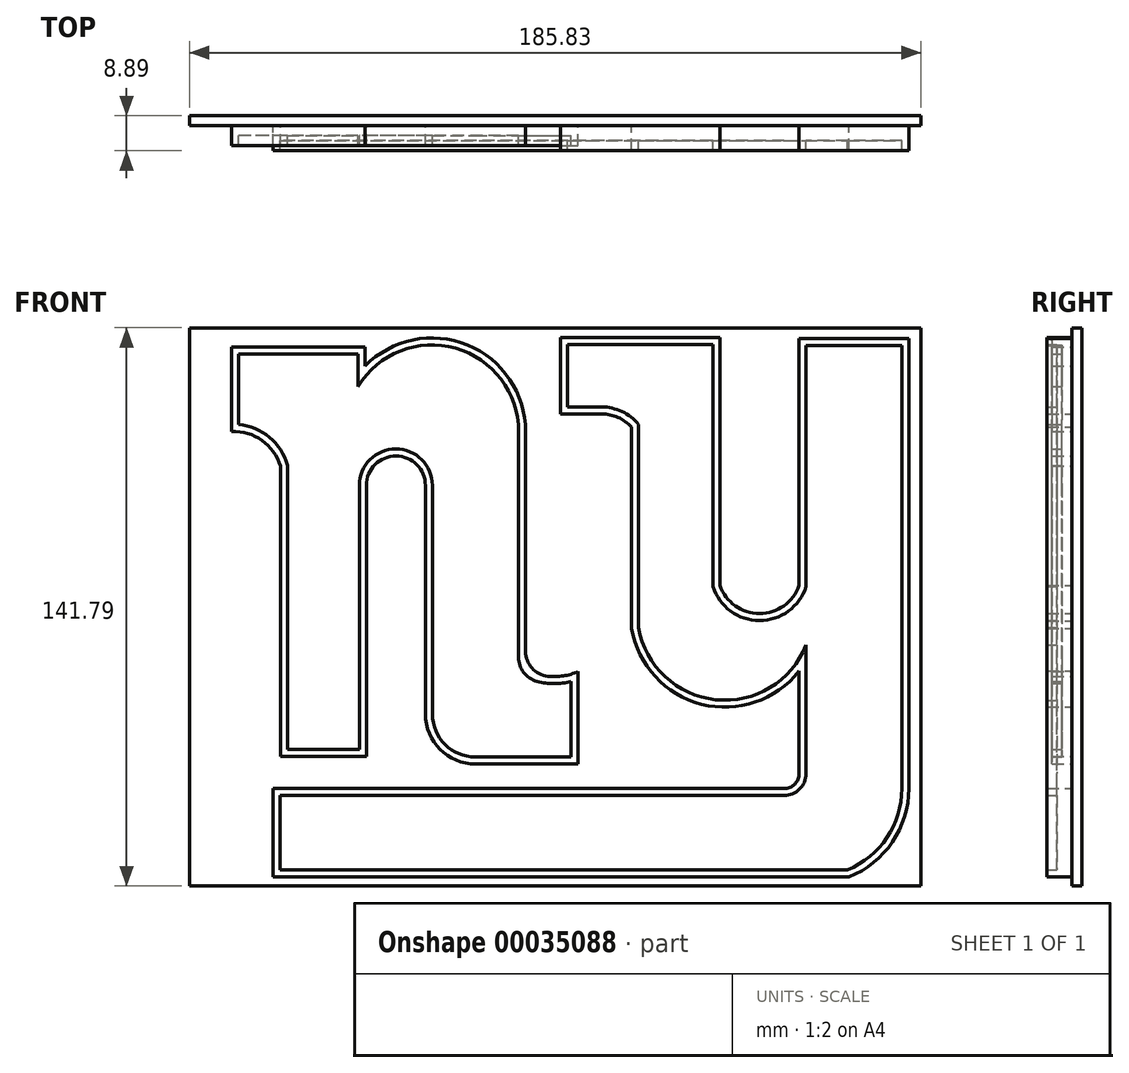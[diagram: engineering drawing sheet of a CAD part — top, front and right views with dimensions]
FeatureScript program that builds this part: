
annotation { "Feature Type Name" : "Feature", "Feature Type Description" : "" }
export const myFeature = defineFeature(function(context is Context, id is Id, definition is map)
    precondition{}
    {
        {
            var Q0;
            Q0=qCreatedBy(makeId("Front.planeOp"),FACE);
            var sketch = newSketch(context, id + "F0", { "sketchPlane" : qUnion([Q0])});
            skLineSegment(sketch, "E0", {"start": v(-67.96, -59.93) * mm, "end": v(61.89, -59.93) * mm});
            skLineSegment(sketch, "E1", {"start": v(-67.96, -59.93) * mm, "end": v(-67.96, -82.39) * mm});
            skLineSegment(sketch, "E2", {"start": v(-67.96, -82.39) * mm, "end": v(78.3, -82.39) * mm});
            skLineSegment(sketch, "E3", {"start": v(65.7, -56.12) * mm, "end": v(65.7, -30.07) * mm});
            skPoint(sketch, "E4.visualSharp", {"position": v(65.7, -59.93) * mm});
            skArc(sketch, "E4.filletArc", {"start": v(61.89, -59.93) * mm, "mid": v(64.58, -58.81) * mm, "end": v(65.7, -56.12) * mm});
            skLineSegment(sketch, "E5", {"start": v(23.13, -19.2) * mm, "end": v(23.13, 31.92) * mm});
            skLineSegment(sketch, "E6", {"start": v(93.56, -59.93) * mm, "end": v(93.56, 54.43) * mm});
            skLineSegment(sketch, "E7", {"start": v(65.7, 54.43) * mm, "end": v(65.7, -8.29) * mm});
            skPoint(sketch, "E7.startSnap0", {"position": v(58.35, 54.43) * mm});
            skLineSegment(sketch, "E8", {"start": v(45.58, 54.7) * mm, "end": v(45.58, -8.29) * mm});
            skArc(sketch, "E9", {"start": v(45.58, -8.29) * mm, "mid": v(55.64, -15.46) * mm, "end": v(65.7, -8.29) * mm});
            skLineSegment(sketch, "E10.trimOffspring", {"start": v(65.7, 54.43) * mm, "end": v(93.56, 54.43) * mm});
            skArc(sketch, "E11", {"start": v(23.13, -17.34) * mm, "mid": v(23.11, -18.27) * mm, "end": v(23.13, -19.2) * mm});
            skPoint(sketch, "E12.orphan", {"position": v(23.13, -30.07) * mm});
            skArc(sketch, "E13", {"start": v(23.13, -19.2) * mm, "mid": v(40.88, -38.5) * mm, "end": v(65.7, -30.07) * mm});
            skLineSegment(sketch, "E14", {"start": v(45.58, 54.7) * mm, "end": v(5.04, 54.7) * mm});
            skLineSegment(sketch, "E15", {"start": v(5.04, 54.7) * mm, "end": v(5.04, 35.27) * mm});
            skLineSegment(sketch, "E16", {"start": v(5.04, 35.27) * mm, "end": v(15.48, 35.27) * mm});
            skArc(sketch, "E17", {"start": v(23.13, 31.92) * mm, "mid": v(19.66, 34.4) * mm, "end": v(15.48, 35.27) * mm});
            skPoint(sketch, "E18.orphan", {"position": v(23.13, 54.43) * mm});
            skArc(sketch, "E19", {"start": v(78.3, -82.39) * mm, "mid": v(89.38, -73.5) * mm, "end": v(93.56, -59.93) * mm});
            skSolve(sketch);
        }
        {
            var Q0;
            Q0 = qSketchRegion(id + "F0", true);
            extrude(context, id + "F1", {"entities" : qUnion([Q0]), "depth" : 3.8 * mm});
        }
        {
            var Q0;
            Q0=makeQuery(id+"F1.opExtrude","CAP_FACE",FACE,{"disambiguationData":[OSD([sQuery(id+"F0.wireOp",EDGE,"E0"),sQuery(id+"F0.wireOp",EDGE,"E1"),sQuery(id+"F0.wireOp",EDGE,"E2"),sQuery(id+"F0.wireOp",EDGE,"E3"),sQuery(id+"F0.wireOp",EDGE,"E4.filletArc"),sQuery(id+"F0.wireOp",EDGE,"E5"),sQuery(id+"F0.wireOp",EDGE,"E6"),sQuery(id+"F0.wireOp",EDGE,"E7"),sQuery(id+"F0.wireOp",EDGE,"E8"),sQuery(id+"F0.wireOp",EDGE,"E9"),sQuery(id+"F0.wireOp",EDGE,"E10.trimOffspring"),sQuery(id+"F0.wireOp",EDGE,"E11"),sQuery(id+"F0.wireOp",EDGE,"E13"),sQuery(id+"F0.wireOp",EDGE,"E14"),sQuery(id+"F0.wireOp",EDGE,"E15"),sQuery(id+"F0.wireOp",EDGE,"E16"),sQuery(id+"F0.wireOp",EDGE,"E17"),sQuery(id+"F0.wireOp",EDGE,"E19")])],"isStart":true});
            var sketch = newSketch(context, id + "F2", { "sketchPlane" : qUnion([Q0])});
            skLineSegment(sketch, "E20.bottom", {"start": v(-96.65, 57.16) * mm, "end": v(89.18, 57.16) * mm});
            skLineSegment(sketch, "E20.top", {"start": v(-96.65, -84.63) * mm, "end": v(89.18, -84.63) * mm});
            skLineSegment(sketch, "E20.left", {"start": v(-96.65, 57.16) * mm, "end": v(-96.65, -84.63) * mm});
            skLineSegment(sketch, "E20.right", {"start": v(89.18, 57.16) * mm, "end": v(89.18, -84.63) * mm});
            skSolve(sketch);
        }
        {
            var Q0;
            Q0 = qSketchRegion(id + "F2", true);
            extrude(context, id + "F3", {"entities" : qUnion([Q0]), "depth" : 2.54 * mm});
        }
        {
            var Q0;
            Q0=makeQuery(id+"F3.opExtrude","CAP_FACE",FACE,{"disambiguationData":[OSD([sQuery(id+"F2.wireOp",EDGE,"E20.bottom"),sQuery(id+"F2.wireOp",EDGE,"E20.top"),sQuery(id+"F2.wireOp",EDGE,"E20.left"),sQuery(id+"F2.wireOp",EDGE,"E20.right")])],"isStart":true});
            var sketch = newSketch(context, id + "F4", { "sketchPlane" : qUnion([Q0])});
            skLineSegment(sketch, "E21", {"start": v(-66.1, -51.73) * mm, "end": v(-44.25, -51.73) * mm});
            skLineSegment(sketch, "E22", {"start": v(-44.25, -51.73) * mm, "end": v(-44.25, 17.1) * mm});
            skLineSegment(sketch, "E23", {"start": v(-66.1, -51.73) * mm, "end": v(-66.1, 21.98) * mm});
            skArc(sketch, "E24", {"start": v(-29.25, 17.1) * mm, "mid": v(-36.75, 24.6) * mm, "end": v(-44.25, 17.1) * mm});
            skLineSegment(sketch, "E25", {"start": v(-29.25, 17.1) * mm, "end": v(-29.25, -40.98) * mm});
            skLineSegment(sketch, "E26", {"start": v(-16.55, -53.68) * mm, "end": v(9.57, -53.68) * mm});
            skPoint(sketch, "E27.visualSharp", {"position": v(-29.25, -53.68) * mm});
            skArc(sketch, "E27.filletArc", {"start": v(-29.25, -40.98) * mm, "mid": v(-25.53, -49.96) * mm, "end": v(-16.55, -53.68) * mm});
            skLineSegment(sketch, "E28", {"start": v(9.57, -53.68) * mm, "end": v(9.57, -30.2) * mm});
            skLineSegment(sketch, "E29", {"start": v(-44.58, 47.42) * mm, "end": v(-44.58, 52.32) * mm});
            skLineSegment(sketch, "E30", {"start": v(-44.58, 52.32) * mm, "end": v(-78.5, 52.32) * mm});
            skLineSegment(sketch, "E31", {"start": v(-78.5, 52.32) * mm, "end": v(-78.5, 30.8) * mm});
            skArc(sketch, "E32", {"start": v(-66.1, 21.98) * mm, "mid": v(-70.77, 28.54) * mm, "end": v(-78.5, 30.8) * mm});
            skArc(sketch, "E33", {"start": v(1.86, -31.38) * mm, "mid": v(5.8, -31.3) * mm, "end": v(9.57, -30.2) * mm});
            skLineSegment(sketch, "E34", {"start": v(-3.8, -25.07) * mm, "end": v(-3.8, 30.8) * mm});
            skArc(sketch, "E35", {"start": v(-3.8, 30.8) * mm, "mid": v(-18.6, 52.8) * mm, "end": v(-44.58, 47.42) * mm});
            skPoint(sketch, "E36.visualSharp", {"position": v(-3.8, -29.6) * mm});
            skArc(sketch, "E36.filletArc", {"start": v(-3.8, -25.07) * mm, "mid": v(-2.18, -29.3) * mm, "end": v(1.86, -31.38) * mm});
            skSolve(sketch);
        }
        {
            var Q0;
            Q0=makeQuery(id+"F4.imprint","IMPRINT",FACE,{"disambiguationData":[TD([[makeQuery(id+"F4.imprint","IMPRINT",EDGE,{"derivedFrom":sQuery(id+"F4.wireOp",EDGE,"E21")}),1.0]])]});
            extrude(context, id + "F5", {"entities" : qUnion([Q0]), "operationType" : NewBodyOperationType.ADD, "depth" : 2.54 * mm});
        }
        {
            var Q0;
            Q0=makeQuery(id+"F5.opExtrude","CAP_FACE",FACE,{"disambiguationData":[OSD([sQuery(id+"F4.wireOp",EDGE,"E21"),sQuery(id+"F4.wireOp",EDGE,"E22"),sQuery(id+"F4.wireOp",EDGE,"E23"),sQuery(id+"F4.wireOp",EDGE,"E24"),sQuery(id+"F4.wireOp",EDGE,"E25"),sQuery(id+"F4.wireOp",EDGE,"E26"),sQuery(id+"F4.wireOp",EDGE,"E27.filletArc"),sQuery(id+"F4.wireOp",EDGE,"E28"),sQuery(id+"F4.wireOp",EDGE,"E29"),sQuery(id+"F4.wireOp",EDGE,"E30"),sQuery(id+"F4.wireOp",EDGE,"E31"),sQuery(id+"F4.wireOp",EDGE,"E32"),sQuery(id+"F4.wireOp",EDGE,"E33"),sQuery(id+"F4.wireOp",EDGE,"E34"),sQuery(id+"F4.wireOp",EDGE,"E35")])],"isStart":false});
            var sketch = newSketch(context, id + "F6", { "sketchPlane" : qUnion([Q0])});
            skArc(sketch, "E37.0", {"start": v(-76.72, 32.54) * mm, "mid": v(-68.9, 29.34) * mm, "end": v(-64.32, 22.23) * mm});
            skLineSegment(sketch, "E37.1", {"start": v(-76.72, 50.54) * mm, "end": v(-76.72, 32.54) * mm});
            skLineSegment(sketch, "E37.2", {"start": v(-46.35, 50.54) * mm, "end": v(-76.72, 50.54) * mm});
            skLineSegment(sketch, "E37.3", {"start": v(-46.35, 42.27) * mm, "end": v(-46.35, 50.54) * mm});
            skLineSegment(sketch, "E37.4", {"start": v(-27.47, 17.1) * mm, "end": v(-27.47, -40.98) * mm});
            skArc(sketch, "E37.5", {"start": v(-46.03, 17.1) * mm, "mid": v(-36.75, 26.37) * mm, "end": v(-27.47, 17.1) * mm});
            skLineSegment(sketch, "E37.6", {"start": v(-46.03, -49.95) * mm, "end": v(-46.03, 17.1) * mm});
            skLineSegment(sketch, "E37.7", {"start": v(-64.32, -49.95) * mm, "end": v(-46.03, -49.95) * mm});
            skArc(sketch, "E37.8", {"start": v(-27.47, -40.98) * mm, "mid": v(-24.27, -48.7) * mm, "end": v(-16.55, -51.9) * mm});
            skLineSegment(sketch, "E37.9", {"start": v(-16.55, -51.9) * mm, "end": v(7.79, -51.9) * mm});
            skLineSegment(sketch, "E37.10", {"start": v(7.79, -51.9) * mm, "end": v(7.79, -32.7) * mm});
            skArc(sketch, "E37.11", {"start": v(7.79, -32.7) * mm, "mid": v(3.46, -33.25) * mm, "end": v(-0.87, -32.68) * mm});
            skLineSegment(sketch, "E37.12", {"start": v(-64.32, 22.23) * mm, "end": v(-64.32, -49.95) * mm});
            skLineSegment(sketch, "E37.13", {"start": v(-5.58, -26.54) * mm, "end": v(-5.58, 30.8) * mm});
            skArc(sketch, "E37.14", {"start": v(-5.58, 30.8) * mm, "mid": v(-21.62, 51.97) * mm, "end": v(-46.35, 42.27) * mm});
            skPoint(sketch, "E38.visualSharp", {"position": v(-5.58, -30.61) * mm});
            skArc(sketch, "E38.filletArc", {"start": v(-5.58, -26.54) * mm, "mid": v(-4.27, -30.4) * mm, "end": v(-0.87, -32.68) * mm});
            skSolve(sketch);
        }
        {
            var Q0;
            Q0=makeQuery(id+"F6.imprint","IMPRINT",FACE,{"disambiguationData":[TD([[makeQuery(id+"F6.imprint","IMPRINT",EDGE,{"derivedFrom":sQuery(id+"F6.wireOp",EDGE,"0f141487-670b-4e59-a937-231628a92157.0")}),1.0]])]});
            var Q1;
            Q1=makeQuery(id+"F6.imprint","IMPRINT",FACE,{"disambiguationData":[TD([[makeQuery(id+"F6.imprint","IMPRINT",EDGE,{"derivedFrom":sQuery(id+"F6.wireOp",EDGE,"E37.0")}),1.0]])]});
            extrude(context, id + "F7", {"entities" : qUnion([Q0, Q1]), "operationType" : NewBodyOperationType.ADD, "depth" : 2.54 * mm});
        }
        {
            var Q0;
            Q0=makeQuery(id+"F1.opExtrude","CAP_FACE",FACE,{"disambiguationData":[OSD([sQuery(id+"F0.wireOp",EDGE,"E0"),sQuery(id+"F0.wireOp",EDGE,"E1"),sQuery(id+"F0.wireOp",EDGE,"E2"),sQuery(id+"F0.wireOp",EDGE,"E3"),sQuery(id+"F0.wireOp",EDGE,"E4.filletArc"),sQuery(id+"F0.wireOp",EDGE,"E5"),sQuery(id+"F0.wireOp",EDGE,"E6"),sQuery(id+"F0.wireOp",EDGE,"E7"),sQuery(id+"F0.wireOp",EDGE,"E8"),sQuery(id+"F0.wireOp",EDGE,"E9"),sQuery(id+"F0.wireOp",EDGE,"E10.trimOffspring"),sQuery(id+"F0.wireOp",EDGE,"E11"),sQuery(id+"F0.wireOp",EDGE,"E13"),sQuery(id+"F0.wireOp",EDGE,"E14"),sQuery(id+"F0.wireOp",EDGE,"E15"),sQuery(id+"F0.wireOp",EDGE,"E16"),sQuery(id+"F0.wireOp",EDGE,"E17"),sQuery(id+"F0.wireOp",EDGE,"E19")])],"isStart":false});
            var sketch = newSketch(context, id + "F8", { "sketchPlane" : qUnion([Q0])});
            skArc(sketch, "E39.0", {"start": v(67.47, -56.12) * mm, "mid": v(65.84, -60.07) * mm, "end": v(61.89, -61.7) * mm});
            skLineSegment(sketch, "E39.1", {"start": v(67.47, -23.48) * mm, "end": v(67.47, -56.12) * mm});
            skArc(sketch, "E39.2", {"start": v(24.9, -19.02) * mm, "mid": v(44.5, -37.34) * mm, "end": v(67.47, -23.48) * mm});
            skArc(sketch, "E39.3", {"start": v(24.9, -17.37) * mm, "mid": v(24.89, -18.2) * mm, "end": v(24.9, -19.02) * mm});
            skLineSegment(sketch, "E39.4", {"start": v(24.9, 32.58) * mm, "end": v(24.9, -17.37) * mm});
            skLineSegment(sketch, "E39.5", {"start": v(61.89, -61.7) * mm, "end": v(-66.18, -61.7) * mm});
            skArc(sketch, "E39.6", {"start": v(15.48, 37.05) * mm, "mid": v(20.7, 35.87) * mm, "end": v(24.9, 32.58) * mm});
            skLineSegment(sketch, "E39.7", {"start": v(6.81, 37.05) * mm, "end": v(15.48, 37.05) * mm});
            skLineSegment(sketch, "E39.8", {"start": v(91.78, -59.93) * mm, "end": v(91.78, 52.65) * mm});
            skArc(sketch, "E39.9", {"start": v(77.95, -80.61) * mm, "mid": v(88, -72.37) * mm, "end": v(91.78, -59.93) * mm});
            skLineSegment(sketch, "E39.10", {"start": v(-66.18, -80.61) * mm, "end": v(77.95, -80.61) * mm});
            skLineSegment(sketch, "E39.11", {"start": v(-66.18, -61.7) * mm, "end": v(-66.18, -80.61) * mm});
            skLineSegment(sketch, "E39.12", {"start": v(91.78, 52.65) * mm, "end": v(67.47, 52.65) * mm});
            skLineSegment(sketch, "E39.13", {"start": v(67.47, 52.65) * mm, "end": v(67.47, -8.58) * mm});
            skArc(sketch, "E39.14", {"start": v(67.47, -8.58) * mm, "mid": v(55.64, -17.23) * mm, "end": v(43.8, -8.58) * mm});
            skLineSegment(sketch, "E39.15", {"start": v(43.8, -8.58) * mm, "end": v(43.8, 52.93) * mm});
            skLineSegment(sketch, "E39.16", {"start": v(43.8, 52.93) * mm, "end": v(6.81, 52.93) * mm});
            skLineSegment(sketch, "E39.17", {"start": v(6.81, 52.93) * mm, "end": v(6.81, 37.05) * mm});
            skSolve(sketch);
        }
        {
            var Q0;
            Q0=makeQuery(id+"F8.imprint","IMPRINT",FACE,{"disambiguationData":[TD([[makeQuery(id+"F8.imprint","IMPRINT",EDGE,{"derivedFrom":sQuery(id+"F8.wireOp",EDGE,"E39.0")}),1.0]])]});
            extrude(context, id + "F9", {"entities" : qUnion([Q0]), "operationType" : NewBodyOperationType.ADD, "depth" : 2.54 * mm});
        }
    });
